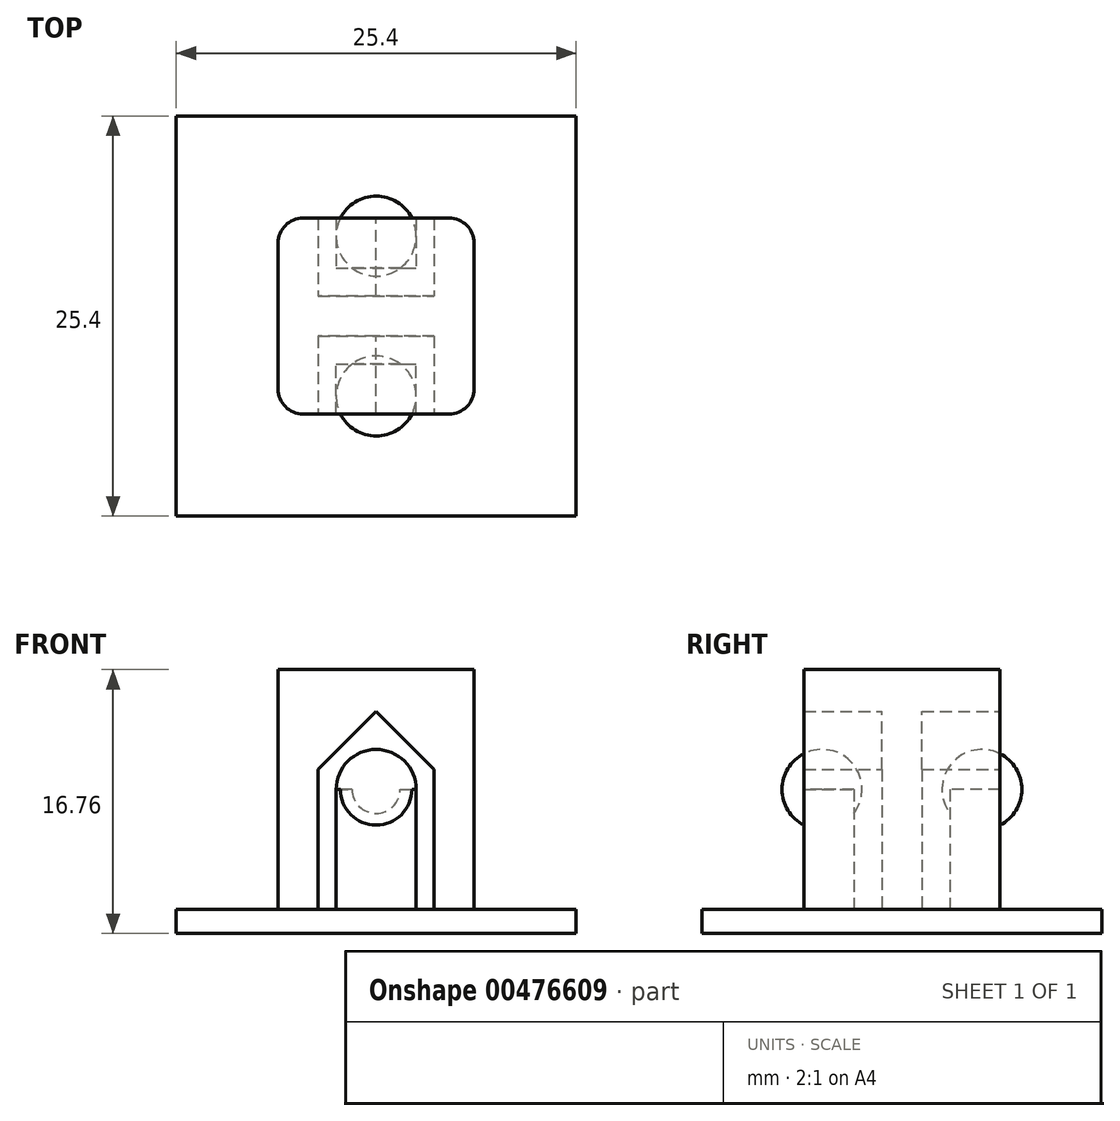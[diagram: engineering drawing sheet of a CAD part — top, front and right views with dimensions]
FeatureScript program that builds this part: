
annotation { "Feature Type Name" : "Feature", "Feature Type Description" : "" }
export const myFeature = defineFeature(function(context is Context, id is Id, definition is map)
    precondition{}
    {
        {
            var Q0;
            Q0=qCreatedBy(makeId("Top.planeOp"),FACE);
            var sketch = newSketch(context, id + "F0", { "sketchPlane" : qUnion([Q0])});
            skLineSegment(sketch, "E0.bottom", {"start": v(12.7, 12.7) * mm, "end": v(-12.7, 12.7) * mm});
            skLineSegment(sketch, "E0.top", {"start": v(12.7, -12.7) * mm, "end": v(-12.7, -12.7) * mm});
            skLineSegment(sketch, "E0.left", {"start": v(12.7, 12.7) * mm, "end": v(12.7, -12.7) * mm});
            skLineSegment(sketch, "E0.right", {"start": v(-12.7, 12.7) * mm, "end": v(-12.7, -12.7) * mm});
            skPoint(sketch, "E0.middle", {"position": v(0, 0) * mm});
            skSolve(sketch);
        }
        {
            var Q0;
            Q0=makeQuery(id+"F0.imprint","IMPRINT",FACE,{"disambiguationData":[TD([[makeQuery(id+"F0.imprint","IMPRINT",EDGE,{"derivedFrom":sQuery(id+"F0.wireOp",EDGE,"E0.bottom")}),1.0]])]});
            extrude(context, id + "F1", {"entities" : qUnion([Q0]), "depth" : 1.52 * mm});
        }
        {
            var Q0;
            Q0=makeQuery(id+"F1.opExtrude","CAP_FACE",FACE,{"disambiguationData":[OSD([sQuery(id+"F0.wireOp",EDGE,"E0.bottom"),sQuery(id+"F0.wireOp",EDGE,"E0.top"),sQuery(id+"F0.wireOp",EDGE,"E0.left"),sQuery(id+"F0.wireOp",EDGE,"E0.right")])],"isStart":false});
            var sketch = newSketch(context, id + "F2", { "sketchPlane" : qUnion([Q0])});
            skLineSegment(sketch, "E1.bottom", {"start": v(6.22, 6.22) * mm, "end": v(3.68, 6.22) * mm});
            skLineSegment(sketch, "E1.top", {"start": v(6.22, -6.22) * mm, "end": v(3.68, -6.22) * mm});
            skLineSegment(sketch, "E1.left", {"start": v(6.22, 6.22) * mm, "end": v(6.22, -6.22) * mm});
            skLineSegment(sketch, "E1.right", {"start": v(-6.22, 6.22) * mm, "end": v(-6.22, -6.22) * mm});
            skPoint(sketch, "E1.middle", {"position": v(0, 0) * mm});
            skLineSegment(sketch, "E2.0", {"start": v(-3.68, 6.22) * mm, "end": v(-3.68, 1.27) * mm});
            skLineSegment(sketch, "E3.0", {"start": v(3.68, 6.22) * mm, "end": v(3.68, 1.27) * mm});
            skLineSegment(sketch, "E4.0", {"start": v(-3.68, -1.27) * mm, "end": v(3.68, -1.27) * mm});
            skLineSegment(sketch, "E5.0", {"start": v(-3.68, 1.27) * mm, "end": v(3.68, 1.27) * mm});
            skPoint(sketch, "E6.orphan", {"position": v(-6.22, 0) * mm});
            skLineSegment(sketch, "E7.trimOffspring", {"start": v(-3.68, -1.27) * mm, "end": v(-3.68, -6.22) * mm});
            skLineSegment(sketch, "E8.trimOffspring", {"start": v(3.68, -1.27) * mm, "end": v(3.68, -6.22) * mm});
            skPoint(sketch, "E9.end.orphan", {"position": v(6.22, 0) * mm});
            skLineSegment(sketch, "E10.trimOffspring", {"start": v(-3.68, 6.22) * mm, "end": v(-6.22, 6.22) * mm});
            skLineSegment(sketch, "E11.trimOffspring", {"start": v(-3.68, -6.22) * mm, "end": v(-6.22, -6.22) * mm});
            skLineSegment(sketch, "E12.bottom", {"start": v(-2.54, 6.22) * mm, "end": v(2.54, 6.22) * mm});
            skLineSegment(sketch, "E12.top", {"start": v(-2.54, 3.05) * mm, "end": v(2.54, 3.05) * mm});
            skLineSegment(sketch, "E12.left", {"start": v(-2.54, 6.22) * mm, "end": v(-2.54, 3.05) * mm});
            skLineSegment(sketch, "E12.right", {"start": v(2.54, 6.22) * mm, "end": v(2.54, 3.05) * mm});
            skLineSegment(sketch, "E13.MirrorCS", {"start": v(2.54, -6.22) * mm, "end": v(2.54, -3.05) * mm});
            skLineSegment(sketch, "E14.MirrorCS", {"start": v(-2.54, -6.22) * mm, "end": v(-2.54, -3.05) * mm});
            skLineSegment(sketch, "E15.MirrorCS", {"start": v(-2.54, -6.22) * mm, "end": v(2.54, -6.22) * mm});
            skLineSegment(sketch, "E16.MirrorCS", {"start": v(-2.54, -3.05) * mm, "end": v(2.54, -3.05) * mm});
            skSolve(sketch);
        }
        {
            var Q0;
            Q0=makeQuery(id+"F2.imprint","IMPRINT",FACE,{"disambiguationData":[TD([[makeQuery(id+"F2.imprint","IMPRINT",EDGE,{"derivedFrom":sQuery(id+"F2.wireOp",EDGE,"E1.bottom")}),1.0]])]});
            extrude(context, id + "F3", {"entities" : qUnion([Q0]), "operationType" : NewBodyOperationType.ADD, "depth" : 15.24 * mm});
        }
        {
            var Q0;
            Q0=makeQuery(id+"F2.imprint","IMPRINT",FACE,{"disambiguationData":[TD([[makeQuery(id+"F2.imprint","IMPRINT",EDGE,{"derivedFrom":sQuery(id+"F2.wireOp",EDGE,"E13.MirrorCS")}),1.0]])]});
            var Q1;
            Q1=makeQuery(id+"F2.imprint","IMPRINT",FACE,{"disambiguationData":[TD([[makeQuery(id+"F2.imprint","IMPRINT",EDGE,{"derivedFrom":sQuery(id+"F2.wireOp",EDGE,"E12.bottom")}),-1.0]])]});
            extrude(context, id + "F4", {"entities" : qUnion([Q0, Q1]), "operationType" : NewBodyOperationType.ADD, "depth" : 7.62 * mm});
        }
        {
            var Q0;
            Q0=makeQuery(id+"F4.opExtrude","CAP_FACE",FACE,{"disambiguationData":[OSD([sQuery(id+"F2.wireOp",EDGE,"E13.MirrorCS"),sQuery(id+"F2.wireOp",EDGE,"E14.MirrorCS"),sQuery(id+"F2.wireOp",EDGE,"E15.MirrorCS"),sQuery(id+"F2.wireOp",EDGE,"E16.MirrorCS")])],"isStart":false});
            var sketch = newSketch(context, id + "F5", { "sketchPlane" : qUnion([Q0])});
            skLineSegment(sketch, "E17", {"start": v(2.54, -5.08) * mm, "end": v(-2.54, -5.08) * mm});
            skArc(sketch, "E18", {"start": v(-2.54, -5.08) * mm, "mid": v(0, -7.62) * mm, "end": v(2.54, -5.08) * mm});
            skLineSegment(sketch, "E19.MirrorCS", {"start": v(2.54, 5.08) * mm, "end": v(-2.54, 5.08) * mm});
            skArc(sketch, "E20.MirrorCS", {"start": v(-2.54, 5.08) * mm, "mid": v(0, 7.62) * mm, "end": v(2.54, 5.08) * mm});
            skSolve(sketch);
        }
        {
            var Q0;
            Q0=makeQuery(id+"F5.imprint","IMPRINT",FACE,{"disambiguationData":[TD([[makeQuery(id+"F5.imprint","IMPRINT",EDGE,{"derivedFrom":sQuery(id+"F5.wireOp",EDGE,"E19.MirrorCS")}),-1.0]])]});
            var Q1;
            Q1=sQuery(id+"F5.wireOp",EDGE,"E19.MirrorCS");
            revolve(context, id + "F6", {"operationType" : NewBodyOperationType.ADD, "entities" : qUnion([Q0]), "axis" : qUnion([Q1]), "revolveType" : RevolveType.FULL});
        }
        {
            var Q0;
            {var subQ0=sQuery(id+"F5.wireOp",EDGE,"E18");var subQ1=makeQuery(id+"F4.opExtrude","CAP_EDGE",EDGE,{"disambiguationData":[OSD([sQuery(id+"F2.wireOp",EDGE,"E15.MirrorCS")])],"isStart":false});var subQ2=makeQuery(id+"F5.imprint","INTERSECT",VERTEX,{"disambiguationData":[OD(0.0)],"derivedFrom":[subQ1,subQ0]});Q0=makeQuery(id+"F5.imprint","IMPRINT",FACE,{"disambiguationData":[TD([[makeQuery(id+"F5.imprint","IMPRINT",EDGE,{"disambiguationData":[TD([[subQ2,-1.0]])],"derivedFrom":subQ0}),1.0]])]});}
            var Q1;
            {var subQ0=sQuery(id+"F5.wireOp",EDGE,"E17");Q1=makeQuery(id+"F5.imprint","IMPRINT",FACE,{"disambiguationData":[TD([[makeQuery(id+"F5.imprint","IMPRINT",EDGE,{"derivedFrom":subQ0}),1.0]])]});}
            var Q2;
            Q2=sQuery(id+"F5.wireOp",EDGE,"E17");
            revolve(context, id + "F7", {"operationType" : NewBodyOperationType.ADD, "entities" : qUnion([Q0, Q1]), "axis" : qUnion([Q2]), "revolveType" : RevolveType.FULL});
        }
        {
            var Q0;
            Q0=makeQuery(id+"F3.opExtrude","SWEPT_FACE",FACE,{"disambiguationData":[OSD([sQuery(id+"F2.wireOp",EDGE,"E1.bottom")])]});
            var sketch = newSketch(context, id + "F8", { "sketchPlane" : qUnion([Q0])});
            skLineSegment(sketch, "E21", {"start": v(-3.68, 10.41) * mm, "end": v(0, 14.1) * mm});
            skLineSegment(sketch, "E22", {"start": v(0, 14.1) * mm, "end": v(3.68, 10.41) * mm});
            skLineSegment(sketch, "E23", {"start": v(-3.68, 10.41) * mm, "end": v(-3.68, 16.76) * mm});
            skLineSegment(sketch, "E24", {"start": v(-3.68, 16.76) * mm, "end": v(3.68, 16.76) * mm});
            skLineSegment(sketch, "E25", {"start": v(3.68, 16.76) * mm, "end": v(3.68, 10.41) * mm});
            skSolve(sketch);
        }
        {
            var Q0;
            Q0=makeQuery(id+"F8.imprint","IMPRINT",FACE,{"disambiguationData":[TD([[makeQuery(id+"F8.imprint","IMPRINT",EDGE,{"derivedFrom":sQuery(id+"F8.wireOp",EDGE,"E21")}),1.0]])]});
            extrude(context, id + "F9", {"entities" : qUnion([Q0]), "operationType" : NewBodyOperationType.ADD, "oppositeDirection" : true, "depth" : 12.45 * mm});
        }
        {
            var Q0;
            Q0=makeQuery(id+"F3.opExtrude","SWEPT_EDGE",EDGE,{"disambiguationData":[OSD([sQuery(id+"F2.wireOp",EDGE,"E1.right"),sQuery(id+"F2.wireOp",EDGE,"E11.trimOffspring")])]});
            var Q1;
            Q1=makeQuery(id+"F3.opExtrude","SWEPT_EDGE",EDGE,{"disambiguationData":[OSD([sQuery(id+"F2.wireOp",EDGE,"E1.right"),sQuery(id+"F2.wireOp",EDGE,"E10.trimOffspring")])]});
            var Q2;
            Q2=makeQuery(id+"F3.opExtrude","SWEPT_EDGE",EDGE,{"disambiguationData":[OSD([sQuery(id+"F2.wireOp",EDGE,"E1.bottom"),sQuery(id+"F2.wireOp",EDGE,"E1.left")])]});
            var Q3;
            Q3=makeQuery(id+"F3.opExtrude","SWEPT_EDGE",EDGE,{"disambiguationData":[OSD([sQuery(id+"F2.wireOp",EDGE,"E1.top"),sQuery(id+"F2.wireOp",EDGE,"E1.left")])]});
            fillet(context, id + "F10", {"entities" : qUnion([Q0, Q1, Q2, Q3]), "radius" : 1.59 * mm, "tangentPropagation" : true, "allowEdgeOverflow" : false});
        }
    });
